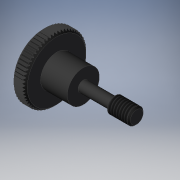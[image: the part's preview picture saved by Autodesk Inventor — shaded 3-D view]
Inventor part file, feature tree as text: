
AUTODESK INVENTOR PART (.ipt)
format: ipt  version: 2019 (Build 230136000, 136)  size: 354,304 bytes
history: native  units: mm
features: sketch x4, revolve x3, thread x1, extrude x1
ambient origin geometry x8: Origin, YZ Plane, XZ Plane, XY Plane, X Axis, Y Axis, Z Axis, Center Point
bodies: Solid1 (feature_tree)
feature tree (9):
  revolve  "Revolution1"  Angle=360.0deg
  revolve  "Revolution2"  [1 undecoded]
  revolve  "Revolution3"  [1 undecoded]
  thread  "Thread1"  [1 undecoded]
  extrude  "Extrusion1"  [1 undecoded]
  sketch  "Sketch_9"
  sketch  "Sketch_3"  dims[d2=360.0deg d3=3.6935mm d4=0.0mm]
  sketch  "Sketch_4"  dims[d5=2.5mm d6=0.0mm]
  sketch  "Sketch_1"  dims[d0=360.0deg d1=360.0deg]
note: 4 required parameter values undecoded (feature->parameter linkage not recoverable at this tier; creation-order binding heuristic only, values carry confidence <= 0.55)